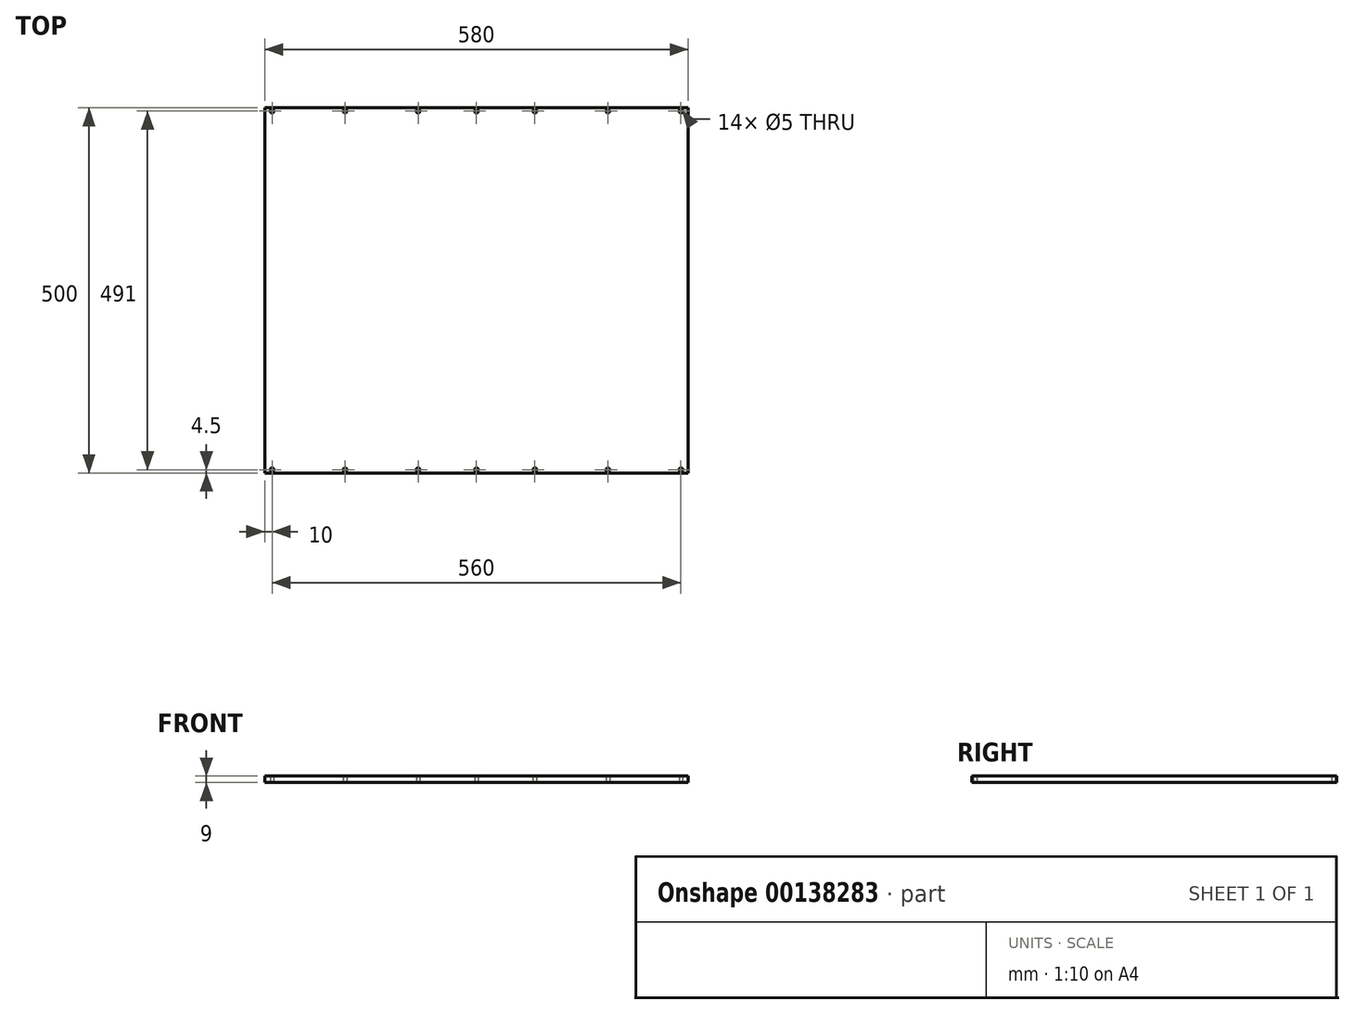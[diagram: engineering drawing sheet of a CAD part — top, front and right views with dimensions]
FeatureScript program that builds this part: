
annotation { "Feature Type Name" : "Feature", "Feature Type Description" : "" }
export const myFeature = defineFeature(function(context is Context, id is Id, definition is map)
    precondition{}
    {
        {
            var Q0;
            Q0=qCreatedBy(makeId("Top.planeOp"),FACE);
            var sketch = newSketch(context, id + "F0", { "sketchPlane" : qUnion([Q0])});
            skLineSegment(sketch, "E0.bottom", {"start": v(290, 250) * mm, "end": v(-290, 250) * mm});
            skLineSegment(sketch, "E0.top", {"start": v(290, -250) * mm, "end": v(-290, -250) * mm});
            skLineSegment(sketch, "E0.left", {"start": v(290, 250) * mm, "end": v(290, -250) * mm});
            skLineSegment(sketch, "E0.right", {"start": v(-290, 250) * mm, "end": v(-290, -250) * mm});
            skPoint(sketch, "E0.middle", {"position": v(0, 0) * mm});
            skLineSegment(sketch, "E1.bottom", {"start": v(-290, -250) * mm, "end": v(290, -250) * mm, "construction": true});
            skLineSegment(sketch, "E1.top", {"start": v(-290, -241) * mm, "end": v(290, -241) * mm, "construction": true});
            skLineSegment(sketch, "E1.left", {"start": v(-290, -250) * mm, "end": v(-290, -241) * mm, "construction": true});
            skLineSegment(sketch, "E1.right", {"start": v(290, -250) * mm, "end": v(290, -241) * mm, "construction": true});
            skLineSegment(sketch, "E2", {"start": v(-290, -245.5) * mm, "end": v(290, -245.5) * mm, "construction": true});
            skCircle(sketch, "E3", {"center": v(0, -245.5) * mm, "radius": 2.5 * mm});
            skCircle(sketch, "E4", {"center": v(-80, -245.5) * mm, "radius": 2.5 * mm});
            skCircle(sketch, "E5", {"center": v(-180, -245.5) * mm, "radius": 2.5 * mm});
            skCircle(sketch, "E6", {"center": v(-280, -245.5) * mm, "radius": 2.5 * mm});
            skLineSegment(sketch, "E7", {"start": v(0, -241) * mm, "end": v(0, -250) * mm, "construction": true});
            skCircle(sketch, "E8.MirrorC", {"center": v(80, -245.5) * mm, "radius": 2.5 * mm});
            skCircle(sketch, "E9.MirrorC", {"center": v(180, -245.5) * mm, "radius": 2.5 * mm});
            skCircle(sketch, "E10.MirrorC", {"center": v(280, -245.5) * mm, "radius": 2.5 * mm});
            skLineSegment(sketch, "E11.MirrorCS", {"start": v(-290, 250) * mm, "end": v(-290, 241) * mm, "construction": true});
            skLineSegment(sketch, "E12.MirrorCS", {"start": v(290, 250) * mm, "end": v(290, 241) * mm, "construction": true});
            skLineSegment(sketch, "E13.MirrorCS", {"start": v(0, 241) * mm, "end": v(0, 250) * mm, "construction": true});
            skCircle(sketch, "E14.MirrorC", {"center": v(0, 245.5) * mm, "radius": 2.5 * mm});
            skCircle(sketch, "E15.MirrorC", {"center": v(180, 245.5) * mm, "radius": 2.5 * mm});
            skCircle(sketch, "E16.MirrorC", {"center": v(80, 245.5) * mm, "radius": 2.5 * mm});
            skCircle(sketch, "E17.MirrorC", {"center": v(280, 245.5) * mm, "radius": 2.5 * mm});
            skCircle(sketch, "E18.MirrorC", {"center": v(-180, 245.5) * mm, "radius": 2.5 * mm});
            skCircle(sketch, "E19.MirrorC", {"center": v(-280, 245.5) * mm, "radius": 2.5 * mm});
            skCircle(sketch, "E20.MirrorC", {"center": v(-80, 245.5) * mm, "radius": 2.5 * mm});
            skLineSegment(sketch, "E21.MirrorCS", {"start": v(-290, 250) * mm, "end": v(290, 250) * mm, "construction": true});
            skLineSegment(sketch, "E22.MirrorCS", {"start": v(-290, 245.5) * mm, "end": v(290, 245.5) * mm, "construction": true});
            skLineSegment(sketch, "E23.MirrorCS", {"start": v(-290, 241) * mm, "end": v(290, 241) * mm, "construction": true});
            skSolve(sketch);
        }
        {
            var Q0;
            Q0=makeQuery(id+"F0.imprint","IMPRINT",FACE,{"disambiguationData":[TD([[makeQuery(id+"F0.imprint","IMPRINT",EDGE,{"derivedFrom":sQuery(id+"F0.wireOp",EDGE,"E0.top")}),-1.0]])]});
            extrude(context, id + "F1", {"entities" : qUnion([Q0]), "depth" : 9 * mm});
        }
    });
